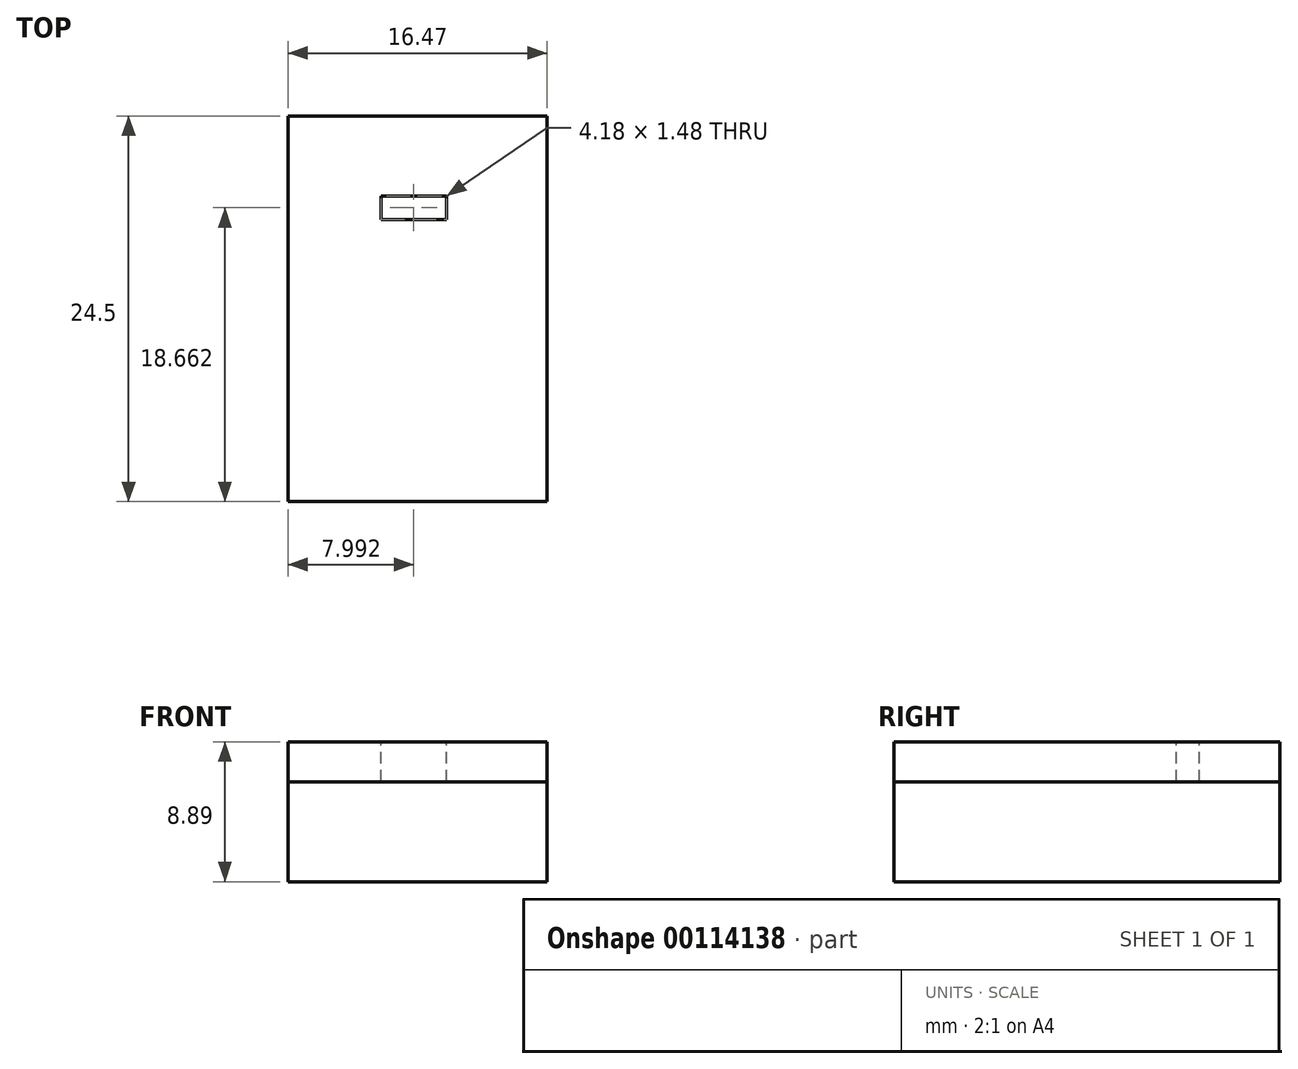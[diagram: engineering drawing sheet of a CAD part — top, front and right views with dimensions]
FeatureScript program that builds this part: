
annotation { "Feature Type Name" : "Feature", "Feature Type Description" : "" }
export const myFeature = defineFeature(function(context is Context, id is Id, definition is map)
    precondition{}
    {
        {
            var Q0;
            Q0=qCreatedBy(makeId("Top.planeOp"),FACE);
            var sketch = newSketch(context, id + "F0", { "sketchPlane" : qUnion([Q0])});
            skLineSegment(sketch, "E0.bottom", {"start": v(-7.99, 12.48) * mm, "end": v(8.48, 12.48) * mm});
            skLineSegment(sketch, "E0.top", {"start": v(-7.99, -12.02) * mm, "end": v(8.48, -12.02) * mm});
            skLineSegment(sketch, "E0.left", {"start": v(-7.99, 12.48) * mm, "end": v(-7.99, -12.02) * mm});
            skLineSegment(sketch, "E0.right", {"start": v(8.48, 12.48) * mm, "end": v(8.48, -12.02) * mm});
            skSolve(sketch);
        }
        {
            var Q0;
            Q0=makeQuery(id+"F0.imprint","IMPRINT",FACE,{"disambiguationData":[TD([[makeQuery(id+"F0.imprint","IMPRINT",EDGE,{"derivedFrom":sQuery(id+"F0.wireOp",EDGE,"E0.bottom")}),-1.0]])]});
            extrude(context, id + "F1", {"entities" : qUnion([Q0]), "depth" : 6.35 * mm});
        }
        {
            var Q0;
            Q0=makeQuery(id+"F1.opExtrude","CAP_FACE",FACE,{"disambiguationData":[OSD([sQuery(id+"F0.wireOp",EDGE,"E0.bottom"),sQuery(id+"F0.wireOp",EDGE,"E0.top"),sQuery(id+"F0.wireOp",EDGE,"E0.left"),sQuery(id+"F0.wireOp",EDGE,"E0.right")])],"isStart":false});
            var sketch = newSketch(context, id + "F2", { "sketchPlane" : qUnion([Q0])});
            skLineSegment(sketch, "E1.bottom", {"start": v(-7.99, 12.48) * mm, "end": v(8.48, 12.48) * mm});
            skLineSegment(sketch, "E1.top", {"start": v(-7.99, -12.02) * mm, "end": v(8.48, -12.02) * mm});
            skLineSegment(sketch, "E1.left", {"start": v(-7.99, 12.48) * mm, "end": v(-7.99, -12.02) * mm});
            skLineSegment(sketch, "E1.right", {"start": v(8.48, 12.48) * mm, "end": v(8.48, -12.02) * mm});
            skSolve(sketch);
        }
        {
            var Q0;
            Q0=qSketchRegion(id+"F2",true);
            var Q1;
            Q1 = qSketchRegion(id + "F4", true);
            extrude(context, id + "F3", {"entities" : qUnion([Q0, Q1]), "depth" : 2.54 * mm});
        }
        {
            var Q0;
            Q0=makeQuery(id+"F3.opExtrude","CAP_FACE",FACE,{"disambiguationData":[OSD([sQuery(id+"F2.wireOp",EDGE,"E1.bottom"),sQuery(id+"F2.wireOp",EDGE,"E1.top"),sQuery(id+"F2.wireOp",EDGE,"E1.left"),sQuery(id+"F2.wireOp",EDGE,"E1.right")])],"isStart":false});
            var sketch = newSketch(context, id + "F4", { "sketchPlane" : qUnion([Q0])});
            skLineSegment(sketch, "E2.bottom", {"start": v(-2.09, 7.38) * mm, "end": v(2.1, 7.38) * mm});
            skLineSegment(sketch, "E2.top", {"start": v(-2.09, 5.9) * mm, "end": v(2.1, 5.9) * mm});
            skLineSegment(sketch, "E2.left", {"start": v(-2.09, 7.38) * mm, "end": v(-2.09, 5.9) * mm});
            skLineSegment(sketch, "E2.right", {"start": v(2.1, 7.38) * mm, "end": v(2.1, 5.9) * mm});
            skSolve(sketch);
        }
        {
            var Q0;
            Q0 = qSketchRegion(id + "F4", true);
            extrude(context, id + "F5", {"entities" : qUnion([Q0]), "operationType" : NewBodyOperationType.REMOVE, "oppositeDirection" : true, "depth" : 2.54 * mm});
        }
    });
